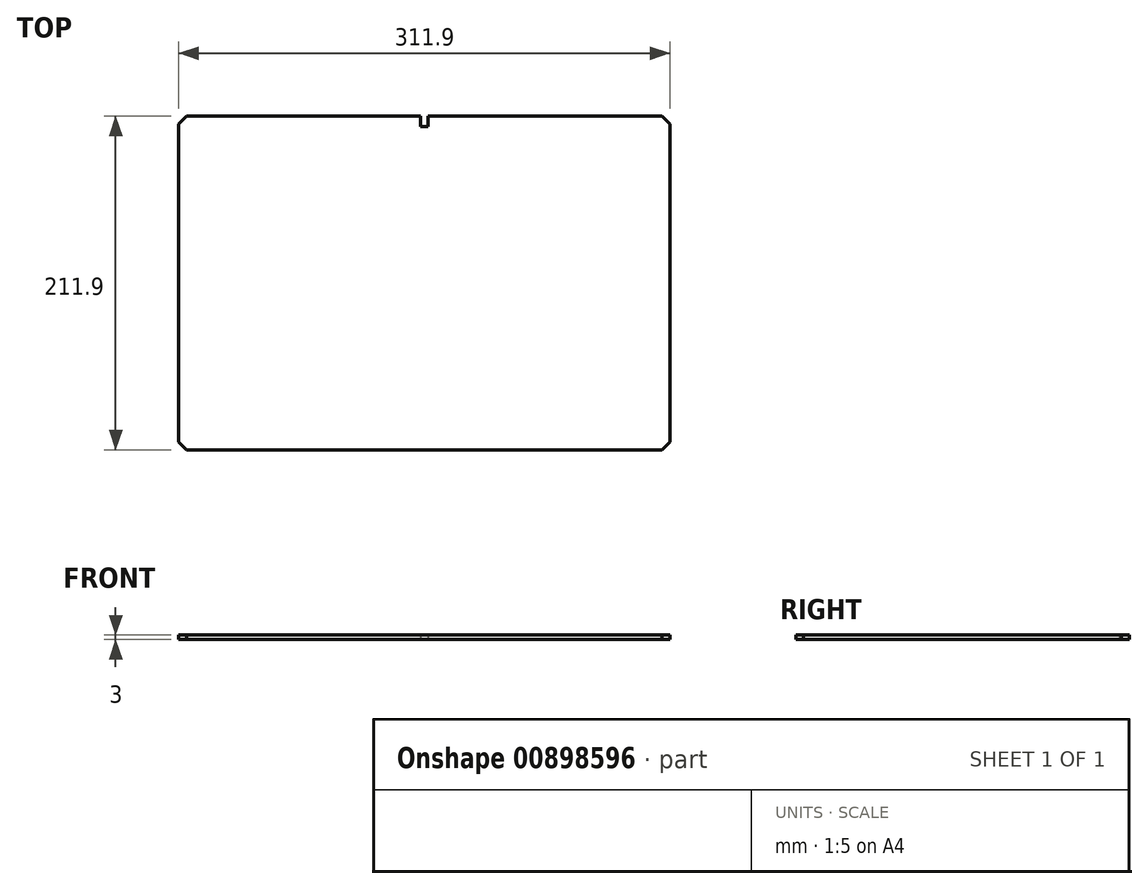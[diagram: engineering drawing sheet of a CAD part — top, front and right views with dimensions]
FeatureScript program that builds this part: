
annotation { "Feature Type Name" : "Feature", "Feature Type Description" : "" }
export const myFeature = defineFeature(function(context is Context, id is Id, definition is map)
    precondition{}
    {
        {
            var Q0;
            Q0=qCreatedBy(makeId("Top.planeOp"),FACE);
            var sketch = newSketch(context, id + "F0", { "sketchPlane" : qUnion([Q0])});
            skLineSegment(sketch, "E0.bottom", {"start": v(552.22, 210.45) * mm, "end": v(861.22, 210.45) * mm, "construction": true});
            skLineSegment(sketch, "E0.top", {"start": v(552.22, 1.45) * mm, "end": v(861.22, 1.45) * mm, "construction": true});
            skLineSegment(sketch, "E0.left", {"start": v(552.22, 210.45) * mm, "end": v(552.22, 1.45) * mm, "construction": true});
            skLineSegment(sketch, "E0.right", {"start": v(861.22, 210.45) * mm, "end": v(861.22, 1.45) * mm, "construction": true});
            skCircle(sketch, "E1", {"center": v(552.22, 210.45) * mm, "radius": 1.45 * mm, "construction": true});
            skCircle(sketch, "E2", {"center": v(861.22, 210.45) * mm, "radius": 1.45 * mm, "construction": true});
            skCircle(sketch, "E3", {"center": v(861.22, 1.45) * mm, "radius": 1.45 * mm, "construction": true});
            skCircle(sketch, "E4", {"center": v(552.22, 1.45) * mm, "radius": 1.45 * mm, "construction": true});
            skLineSegment(sketch, "E5", {"start": v(550.77, 206.9) * mm, "end": v(555.77, 211.9) * mm});
            skLineSegment(sketch, "E6", {"start": v(857.67, 211.9) * mm, "end": v(862.67, 206.9) * mm});
            skLineSegment(sketch, "E7", {"start": v(862.67, 5) * mm, "end": v(857.67, 0) * mm});
            skLineSegment(sketch, "E8", {"start": v(550.77, 5) * mm, "end": v(555.77, 0) * mm});
            skLineSegment(sketch, "E9", {"start": v(555.77, 0) * mm, "end": v(857.67, 0) * mm});
            skLineSegment(sketch, "E10", {"start": v(862.67, 5) * mm, "end": v(862.67, 206.9) * mm});
            skLineSegment(sketch, "E11", {"start": v(857.67, 211.9) * mm, "end": v(709.22, 211.9) * mm});
            skLineSegment(sketch, "E12", {"start": v(550.77, 206.9) * mm, "end": v(550.77, 5) * mm});
            skLineSegment(sketch, "E13", {"start": v(706.72, 210.45) * mm, "end": v(706.72, 205.45) * mm, "construction": true});
            skLineSegment(sketch, "E14", {"start": v(704.22, 205.45) * mm, "end": v(704.22, 211.9) * mm});
            skLineSegment(sketch, "E15", {"start": v(704.22, 205.45) * mm, "end": v(709.22, 205.45) * mm});
            skLineSegment(sketch, "E16", {"start": v(709.22, 205.45) * mm, "end": v(709.22, 211.9) * mm});
            skLineSegment(sketch, "E17.trimOffspring", {"start": v(704.22, 211.9) * mm, "end": v(555.77, 211.9) * mm});
            skSolve(sketch);
        }
        {
            var Q0;
            Q0=qSketchRegion(id+"F0",true);
            extrude(context, id + "F1", {"entities" : qUnion([Q0]), "depth" : 3 * mm});
        }
    });
